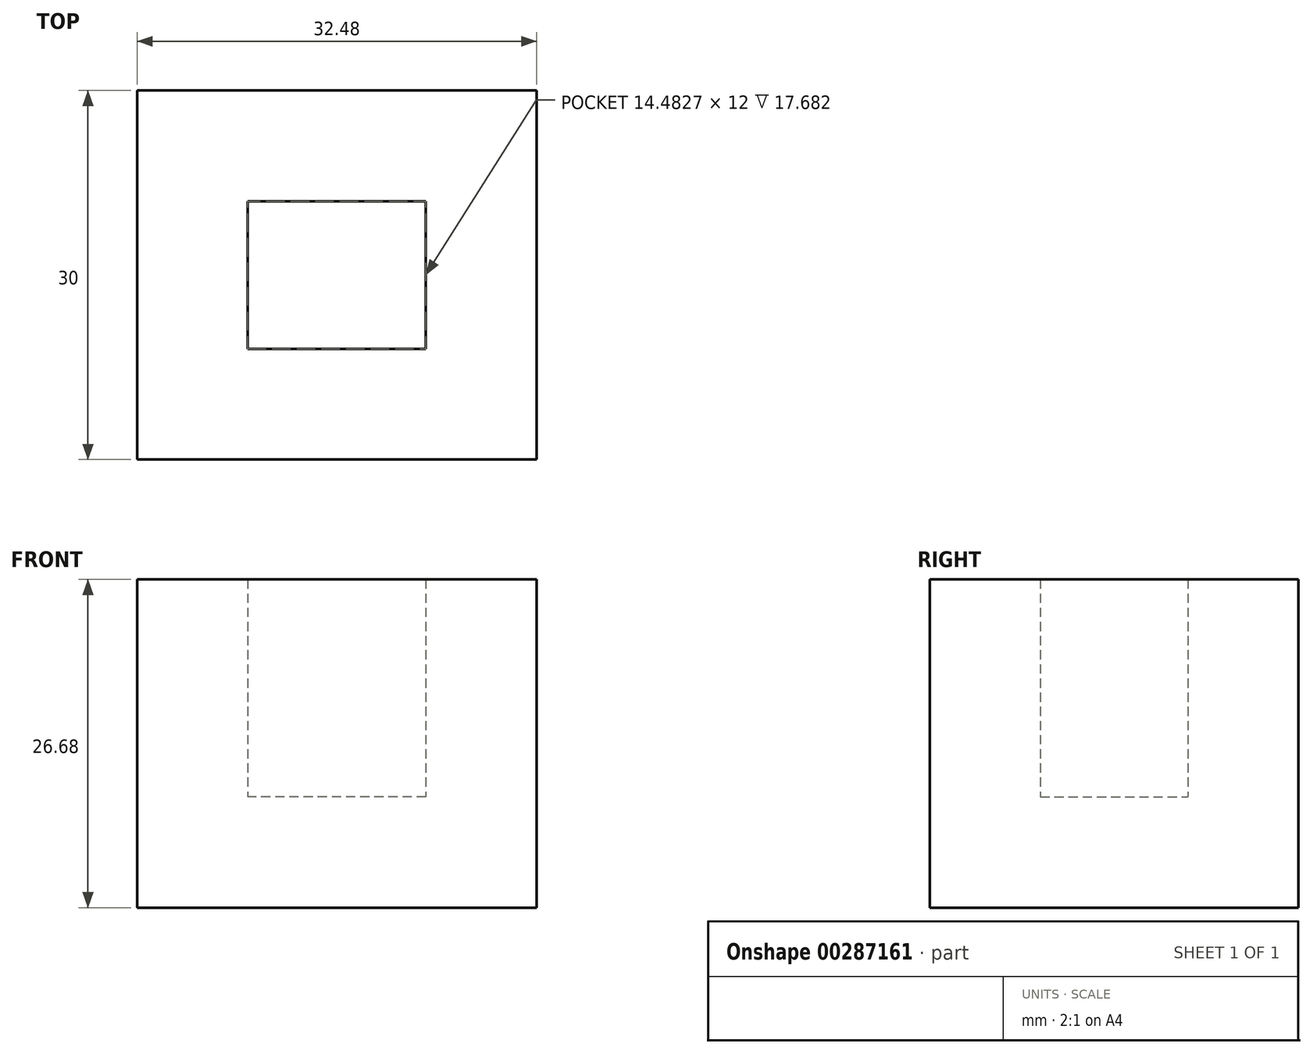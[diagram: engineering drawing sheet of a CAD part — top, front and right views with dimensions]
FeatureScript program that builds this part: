
annotation { "Feature Type Name" : "Feature", "Feature Type Description" : "" }
export const myFeature = defineFeature(function(context is Context, id is Id, definition is map)
    precondition{}
    {
        {
            var Q0;
            Q0=qCreatedBy(makeId("Front.planeOp"),FACE);
            var sketch = newSketch(context, id + "F0", { "sketchPlane" : qUnion([Q0])});
            skLineSegment(sketch, "E0.bottom", {"start": v(35.24, 34.95) * mm, "end": v(2.76, 34.95) * mm});
            skLineSegment(sketch, "E0.top", {"start": v(35.24, 8.27) * mm, "end": v(2.76, 8.27) * mm});
            skLineSegment(sketch, "E0.left", {"start": v(35.24, 34.95) * mm, "end": v(35.24, 8.27) * mm});
            skLineSegment(sketch, "E0.right", {"start": v(2.76, 34.95) * mm, "end": v(2.76, 8.27) * mm});
            skPoint(sketch, "E0.middle", {"position": v(19, 21.6) * mm});
            skSolve(sketch);
        }
        {
            var Q0;
            Q0 = qSketchRegion(id + "F0", true);
            extrude(context, id + "F1", {"entities" : qUnion([Q0]), "depth" : 30 * mm});
        }
        {
            var Q0;
            Q0=makeQuery(id+"F1.opExtrude","SWEPT_FACE",FACE,{"disambiguationData":[OSD([sQuery(id+"F0.wireOp",EDGE,"E0.bottom")])]});
            var Q1;
            Q1=makeQuery(id+"F1.opExtrude","SWEPT_BODY",BODY,{"disambiguationData":[OSD([sQuery(id+"F0.wireOp",EDGE,"E0.bottom"),sQuery(id+"F0.wireOp",EDGE,"E0.top"),sQuery(id+"F0.wireOp",EDGE,"E0.left"),sQuery(id+"F0.wireOp",EDGE,"E0.right")])]});
            shell(context, id + "F2", {"entities" : qUnion([Q0]), "parts" : qUnion([Q1]), "thickness" : 9 * mm});
        }
    });
